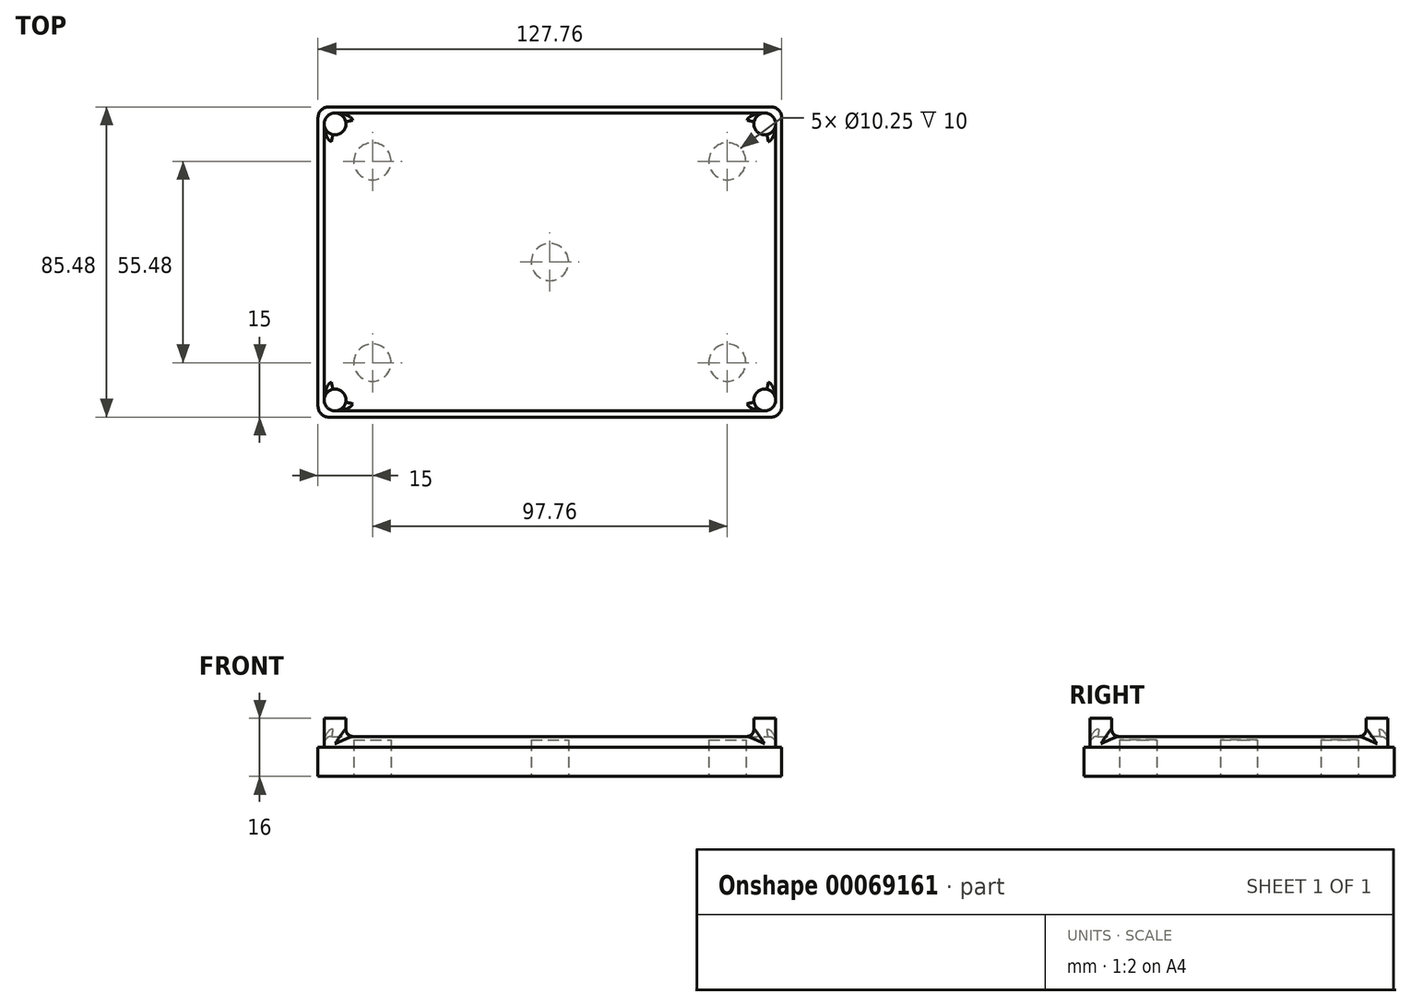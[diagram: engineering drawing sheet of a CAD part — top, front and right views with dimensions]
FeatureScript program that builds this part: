
annotation { "Feature Type Name" : "Feature", "Feature Type Description" : "" }
export const myFeature = defineFeature(function(context is Context, id is Id, definition is map)
    precondition{}
    {
        {
            var Q0;
            Q0=qCreatedBy(makeId("Top.planeOp"),FACE);
            var sketch = newSketch(context, id + "F0", { "sketchPlane" : qUnion([Q0])});
            skLineSegment(sketch, "E0.rect.bottom", {"start": v(63.88, -42.74) * mm, "end": v(-63.88, -42.74) * mm});
            skLineSegment(sketch, "E0.rect.top", {"start": v(63.88, 42.74) * mm, "end": v(-63.88, 42.74) * mm});
            skLineSegment(sketch, "E0.rect.left", {"start": v(63.88, -42.74) * mm, "end": v(63.88, 42.74) * mm});
            skLineSegment(sketch, "E0.rect.right", {"start": v(-63.88, -42.74) * mm, "end": v(-63.88, 42.74) * mm});
            skPoint(sketch, "E0.rect.middle", {"position": v(0, 0) * mm});
            skSolve(sketch);
        }
        {
            var Q0;
            Q0=qSketchRegion(id+"F0",true);
            extrude(context, id + "F1", {"entities" : qUnion([Q0]), "depth" : 8 * mm});
        }
        {
            var Q0;
            Q0=makeQuery(id+"F1.opExtrude","CAP_FACE",FACE,{"disambiguationData":[OSD([sQuery(id+"F0.wireOp",EDGE,"E0.rect.bottom"),sQuery(id+"F0.wireOp",EDGE,"E0.rect.top"),sQuery(id+"F0.wireOp",EDGE,"E0.rect.left"),sQuery(id+"F0.wireOp",EDGE,"E0.rect.right")])],"isStart":false});
            var sketch = newSketch(context, id + "F2", { "sketchPlane" : qUnion([Q0])});
            skSolve(sketch);
        }
        {
            var Q0;
            Q0=makeQuery(id+"F2.imprint","IMPRINT",FACE,{"disambiguationData":[TD([[makeQuery(id+"F2.imprint","IMPRINT",EDGE,{"derivedFrom":makeQuery(id+"F1.opExtrude","CAP_EDGE",EDGE,{"disambiguationData":[OSD([sQuery(id+"F0.wireOp",EDGE,"E0.rect.bottom")])],"isStart":false})}),-1.0]])]});
            var sketch = newSketch(context, id + "F3", { "sketchPlane" : qUnion([Q0])});
            skLineSegment(sketch, "E1.rect.bottom", {"start": v(62.18, -41.04) * mm, "end": v(-62.18, -41.04) * mm});
            skLineSegment(sketch, "E1.rect.top", {"start": v(62.18, 41.04) * mm, "end": v(-62.18, 41.04) * mm});
            skLineSegment(sketch, "E1.rect.left", {"start": v(62.18, -41.04) * mm, "end": v(62.18, 41.04) * mm});
            skLineSegment(sketch, "E1.rect.right", {"start": v(-62.18, -41.04) * mm, "end": v(-62.18, 41.04) * mm});
            skPoint(sketch, "E1.rect.middle", {"position": v(0, 0) * mm});
            skSolve(sketch);
        }
        {
            var Q0;
            Q0=qSketchRegion(id+"F3",true);
            extrude(context, id + "F4", {"entities" : qUnion([Q0]), "operationType" : NewBodyOperationType.ADD, "depth" : 8 * mm});
        }
        {
            var Q0;
            Q0=makeQuery(id+"F1.opExtrude","SWEPT_EDGE",EDGE,{"disambiguationData":[OSD([sQuery(id+"F0.wireOp",EDGE,"E0.rect.top"),sQuery(id+"F0.wireOp",EDGE,"E0.rect.right")])]});
            var Q1;
            Q1=makeQuery(id+"F1.opExtrude","SWEPT_EDGE",EDGE,{"disambiguationData":[OSD([sQuery(id+"F0.wireOp",EDGE,"E0.rect.bottom"),sQuery(id+"F0.wireOp",EDGE,"E0.rect.right")])]});
            var Q2;
            Q2=makeQuery(id+"F1.opExtrude","SWEPT_EDGE",EDGE,{"disambiguationData":[OSD([sQuery(id+"F0.wireOp",EDGE,"E0.rect.bottom"),sQuery(id+"F0.wireOp",EDGE,"E0.rect.left")])]});
            var Q3;
            Q3=makeQuery(id+"F1.opExtrude","SWEPT_EDGE",EDGE,{"disambiguationData":[OSD([sQuery(id+"F0.wireOp",EDGE,"E0.rect.top"),sQuery(id+"F0.wireOp",EDGE,"E0.rect.left")])]});
            var Q4;
            {var subQ0=sQuery(id+"F3.wireOp",EDGE,"E1.rect.right");Q4=makeQuery(id+"FH9UNWzCALQfcbK_1.opChamfer","BLEND_EDGE",EDGE,{"blendedFrom":[makeQuery(id+"F4.opExtrude","SWEPT_EDGE",EDGE,{"disambiguationData":[OSD([sQuery(id+"F3.wireOp",EDGE,"E1.rect.top"),subQ0])]}),makeQuery(id+"F4.opExtrude","SWEPT_FACE",FACE,{"disambiguationData":[OSD([subQ0])]})],"blendedInto":[makeQuery(id+"F4.opExtrude","SWEPT_FACE",FACE,{"disambiguationData":[OSD([subQ0])]})]});}
            var Q5;
            Q5=makeQuery(id+"F4.opExtrude","SWEPT_EDGE",EDGE,{"disambiguationData":[OSD([sQuery(id+"F3.wireOp",EDGE,"E1.rect.bottom"),sQuery(id+"F3.wireOp",EDGE,"E1.rect.right")])]});
            var Q6;
            Q6=makeQuery(id+"F4.opExtrude","SWEPT_EDGE",EDGE,{"disambiguationData":[OSD([sQuery(id+"F3.wireOp",EDGE,"E1.rect.bottom"),sQuery(id+"F3.wireOp",EDGE,"E1.rect.left")])]});
            var Q7;
            Q7=makeQuery(id+"F4.opExtrude","SWEPT_EDGE",EDGE,{"disambiguationData":[OSD([sQuery(id+"F3.wireOp",EDGE,"E1.rect.top"),sQuery(id+"F3.wireOp",EDGE,"E1.rect.left")])]});
            var Q8;
            {var subQ0=sQuery(id+"F3.wireOp",EDGE,"E1.rect.top");Q8=makeQuery(id+"FH9UNWzCALQfcbK_1.opChamfer","BLEND_EDGE",EDGE,{"blendedFrom":[makeQuery(id+"F4.opExtrude","SWEPT_EDGE",EDGE,{"disambiguationData":[OSD([subQ0,sQuery(id+"F3.wireOp",EDGE,"E1.rect.right")])]}),makeQuery(id+"F4.opExtrude","SWEPT_FACE",FACE,{"disambiguationData":[OSD([subQ0])]})],"blendedInto":[makeQuery(id+"F4.opExtrude","SWEPT_FACE",FACE,{"disambiguationData":[OSD([subQ0])]})]});}
            var Q9;
            Q9=makeQuery(id+"F4.opExtrude","SWEPT_EDGE",EDGE,{"disambiguationData":[OSD([sQuery(id+"F3.wireOp",EDGE,"E1.rect.top"),sQuery(id+"F3.wireOp",EDGE,"E1.rect.right")])]});
            fillet(context, id + "F5", {"entities" : qUnion([Q0, Q1, Q2, Q3, Q4, Q5, Q6, Q7, Q8, Q9]), "radius" : 3 * mm, "tangentPropagation" : true, "allowEdgeOverflow" : false});
        }
        {
            var Q0;
            Q0=makeQuery(id+"F1.opExtrude","CAP_FACE",FACE,{"disambiguationData":[OSD([sQuery(id+"F0.wireOp",EDGE,"E0.rect.bottom"),sQuery(id+"F0.wireOp",EDGE,"E0.rect.top"),sQuery(id+"F0.wireOp",EDGE,"E0.rect.left"),sQuery(id+"F0.wireOp",EDGE,"E0.rect.right")])],"isStart":true});
            var sketch = newSketch(context, id + "F6", { "sketchPlane" : qUnion([Q0])});
            skCircle(sketch, "E2", {"center": v(0, 0) * mm, "radius": 5.12 * mm});
            skCircle(sketch, "E3", {"center": v(48.88, 27.74) * mm, "radius": 5.12 * mm});
            skCircle(sketch, "E4", {"center": v(48.88, -27.74) * mm, "radius": 5.12 * mm});
            skCircle(sketch, "E5", {"center": v(-48.88, -27.74) * mm, "radius": 5.12 * mm});
            skCircle(sketch, "E6", {"center": v(-48.88, 27.74) * mm, "radius": 5.12 * mm});
            skSolve(sketch);
        }
        {
            var Q0;
            Q0=makeQuery(id+"F4.opExtrude","CAP_FACE",FACE,{"disambiguationData":[OSD([sQuery(id+"F3.wireOp",EDGE,"E1.rect.bottom"),sQuery(id+"F3.wireOp",EDGE,"E1.rect.top"),sQuery(id+"F3.wireOp",EDGE,"E1.rect.left"),sQuery(id+"F3.wireOp",EDGE,"E1.rect.right")])],"isStart":false});
            var sketch = newSketch(context, id + "F7", { "sketchPlane" : qUnion([Q0])});
            skLineSegment(sketch, "E7", {"start": v(59.18, -41.04) * mm, "end": v(-59.18, -41.04) * mm});
            skArc(sketch, "E8", {"start": v(62.18, -38.04) * mm, "mid": v(57.06, -35.92) * mm, "end": v(59.18, -41.04) * mm});
            skLineSegment(sketch, "E9", {"start": v(62.18, -38.04) * mm, "end": v(62.18, 38.04) * mm});
            skArc(sketch, "E10", {"start": v(59.18, 41.04) * mm, "mid": v(57.06, 35.92) * mm, "end": v(62.18, 38.04) * mm});
            skLineSegment(sketch, "E11", {"start": v(59.18, 41.04) * mm, "end": v(-59.18, 41.04) * mm});
            skArc(sketch, "E12", {"start": v(-62.18, 38.04) * mm, "mid": v(-57.06, 35.92) * mm, "end": v(-59.18, 41.04) * mm});
            skLineSegment(sketch, "E13", {"start": v(-62.18, -38.04) * mm, "end": v(-62.18, 38.04) * mm});
            skArc(sketch, "E14", {"start": v(-59.18, -41.04) * mm, "mid": v(-57.06, -35.92) * mm, "end": v(-62.18, -38.04) * mm});
            skSolve(sketch);
        }
        {
            var Q0;
            Q0 = qSketchRegion(id + "F7", true);
            var Q1;
            Q1=makeQuery(id+"F1.opExtrude","CAP_FACE",FACE,{"disambiguationData":[OSD([sQuery(id+"F0.wireOp",EDGE,"E0.rect.bottom"),sQuery(id+"F0.wireOp",EDGE,"E0.rect.top"),sQuery(id+"F0.wireOp",EDGE,"E0.rect.left"),sQuery(id+"F0.wireOp",EDGE,"E0.rect.right")])],"isStart":false});
            extrude(context, id + "F8", {"entities" : qUnion([Q0]), "operationType" : NewBodyOperationType.REMOVE, "oppositeDirection" : true, "endBoundEntityFace" : qUnion([Q1]), "depth" : 5 * mm});
        }
        {
            var Q0;
            Q0=qSketchRegion(id+"F6",true);
            extrude(context, id + "F9", {"entities" : qUnion([Q0]), "operationType" : NewBodyOperationType.REMOVE, "oppositeDirection" : true, "depth" : 10 * mm});
        }
        {
            var Q0;
            Q0=makeQuery(id+"F8.boolean.opBoolean","COPY",FACE,{"derivedFrom":makeQuery(id+"F8.opExtrude","CAP_FACE",FACE,{"disambiguationData":[OSD([sQuery(id+"F7.wireOp",EDGE,"E7"),sQuery(id+"F7.wireOp",EDGE,"E8"),sQuery(id+"F7.wireOp",EDGE,"E9"),sQuery(id+"F7.wireOp",EDGE,"E10"),sQuery(id+"F7.wireOp",EDGE,"E11"),sQuery(id+"F7.wireOp",EDGE,"E12"),sQuery(id+"F7.wireOp",EDGE,"E13"),sQuery(id+"F7.wireOp",EDGE,"E14")])],"isStart":false})});
            fillet(context, id + "F10", {"entities" : qUnion([Q0]), "radius" : 2 * mm, "tangentPropagation" : true, "allowEdgeOverflow" : false});
        }
    });
